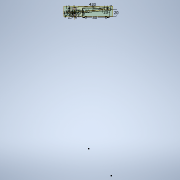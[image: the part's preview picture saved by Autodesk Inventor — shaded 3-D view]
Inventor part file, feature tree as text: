
AUTODESK INVENTOR PART (.ipt)
format: ipt  version: 2020.3 (Build 243373000, 373)  size: 427,008 bytes
history: native  units: mm
features: fillet x9, hole x4, plane x3, extrude x2, sketch x1, chamfer x1
ambient origin geometry x8: Origin, YZ Plane, XZ Plane, XY Plane, X Axis, Y Axis, Z Axis, Center Point
bodies: Solid1 (feature_tree)
feature tree (20):
  sketch  "Sketch1"  dims[d4=6.0mm d5=24.6mm d6=12.4mm d7=6.0mm d15=7.0mm d17=9.0mm d21=20.0mm d23=80.0mm d24=20.0mm d29=29.670597mm d30=6.0mm d31=10.0mm d33=6.0mm d34=0.0mm d40=3.0mm d41=3.0mm d42=2.0mm d43=4.0mm d44=3.0mm d45=4.0mm d50=13.0mm d51=12.0mm d52=22.68928mm d54=1.9mm d55=50.8mm d56=4.0mm d57=2.0mm d58=90.0deg d59=8.0mm d60=20.594885mm d61=0.5mm d62=2.2mm d63=4.0mm d64=4.0mm d65=2.0mm d66=90.0deg d67=8.0mm d68=20.594885mm d69=20.92mm d70=0.0mm d71=2.0mm d80=3.0mm d81=2.0mm d82=45.0deg d87=0.5mm d88=0.5mm d89=6.8mm d90=28.4mm d99=3.0mm d100=6.0mm d101=4.0mm d102=2.0mm d103=90.0deg d104=4.3mm d105=0.0mm d107=420.0mm d108=4.0mm d109=4.0mm d110=6.0mm d111=2.0mm d112=2.0mm d113=0.5mm d114=2.1mm d115=6.0mm d116=4.0mm d117=2.0mm d118=90.0deg d119=7.3mm d120=0.0mm d121=90.0deg d122=90.0deg d123=-7.5mm]
  extrude  "Extrusion1"  Depth=7.3mm
  fillet  "Fillet1"  Radius=12.4mm
  fillet  "Fillet2"  Radius=6.0mm
  fillet  "Fillet3"  Radius=7.0mm
  hole  "Hole1"  [1 undecoded]
  fillet  "Fillet4"  Radius=20.0mm
  hole  "Hole2"  [1 undecoded]
  extrude  "Extrusion3"  Depth=7.3mm
  hole  "Hole5"  [1 undecoded]
  fillet  "Fillet5"  Radius=6.0mm
  chamfer  "Chamfer2"  Distance=10.0mm
  fillet  "Fillet8"  Radius=6.0mm
  fillet  "Fillet10"  Radius=3.0mm
  fillet  "Fillet9"  Radius=3.0mm
  fillet  "Fillet11"  Radius=2.0mm
  hole  "Hole6"  [1 undecoded]
  plane  "Work Plane1"
  plane  "Work Plane2"
  plane  "Work Plane3"
note: 4 required parameter values undecoded (feature->parameter linkage not recoverable at this tier; creation-order binding heuristic only, values carry confidence <= 0.55)
